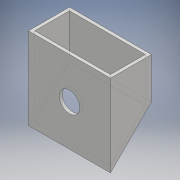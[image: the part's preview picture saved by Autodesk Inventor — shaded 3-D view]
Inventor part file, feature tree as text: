
AUTODESK INVENTOR PART (.ipt)
format: ipt  version: 2018 (Build 220112000, 112)  size: 105,984 bytes
history: native  units: mm
features: sketch x2, other x1, extrude x1, chamfer x1, hole x1
ambient origin geometry x8: Origin, YZ Plane, XZ Plane, XY Plane, X Axis, Y Axis, Z Axis, Center Point
bodies: Body1 (feature_tree)
feature tree (6):
  other  "ソリッド1"
  extrude  "押し出し1"  Depth=60.0mm
  chamfer  "面取り1"  Distance=30.0mm
  hole  "穴1"  [1 undecoded]
  sketch  "スケッチ1"
  sketch  "スケッチ2"
note: 1 required parameter value undecoded (feature->parameter linkage not recoverable at this tier; creation-order binding heuristic only, values carry confidence <= 0.55)
